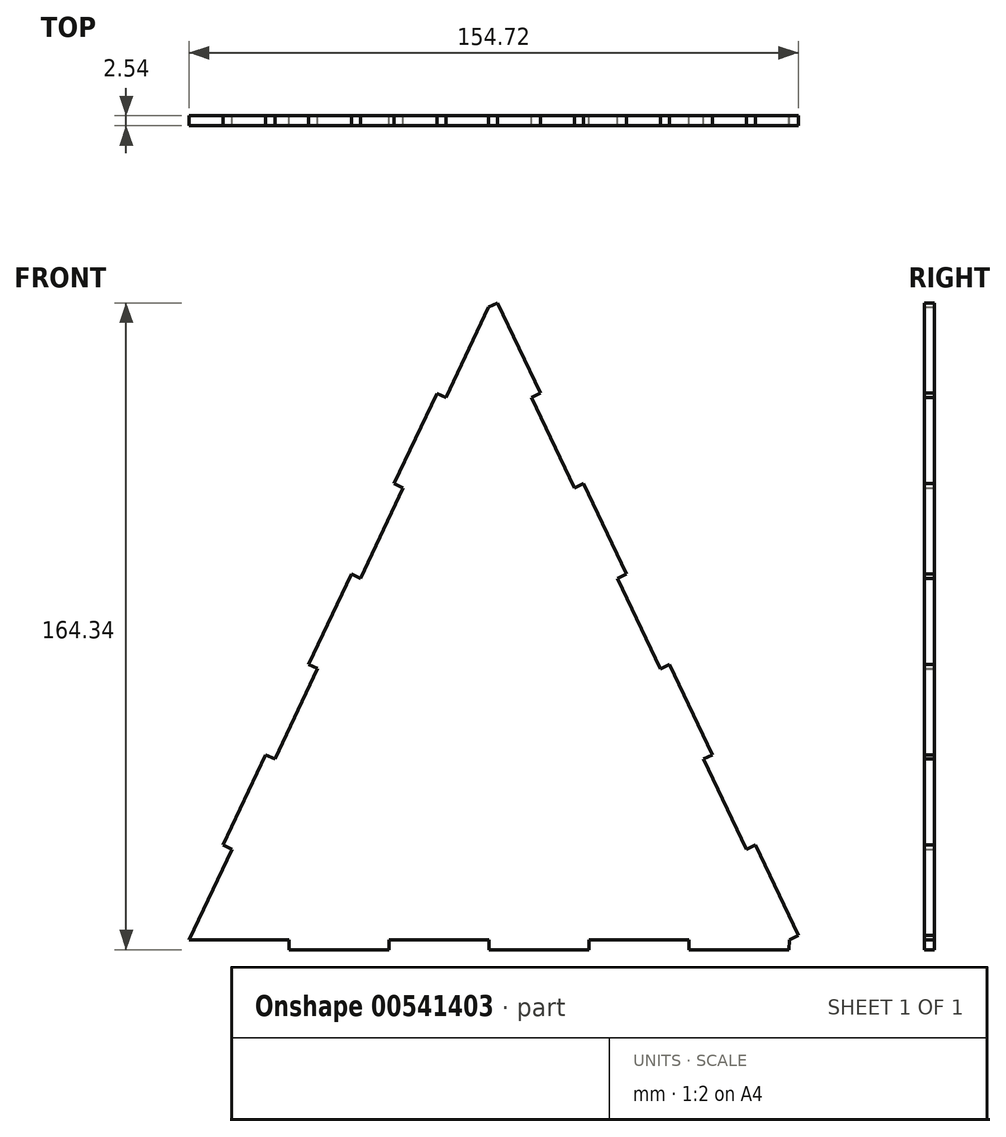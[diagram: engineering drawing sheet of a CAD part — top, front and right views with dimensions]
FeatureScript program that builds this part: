
annotation { "Feature Type Name" : "Feature", "Feature Type Description" : "" }
export const myFeature = defineFeature(function(context is Context, id is Id, definition is map)
    precondition{}
    {
        {
            var Q0;
            Q0=qCreatedBy(makeId("Front.planeOp"),FACE);
            var sketch = newSketch(context, id + "F0", { "sketchPlane" : qUnion([Q0])});
            skLineSegment(sketch, "E0", {"start": v(0, 85.84) * mm, "end": v(-76.07, -74.87) * mm});
            skLineSegment(sketch, "E1", {"start": v(-76.07, -74.87) * mm, "end": v(76.36, -74.87) * mm});
            skLineSegment(sketch, "E2", {"start": v(65.46, -51.93) * mm, "end": v(32.75, 16.9) * mm});
            skLineSegment(sketch, "E3", {"start": v(0, 85.84) * mm, "end": v(-10.87, 62.88) * mm});
            skLineSegment(sketch, "E4", {"start": v(-10.87, 62.88) * mm, "end": v(-13.16, 63.97) * mm});
            skLineSegment(sketch, "E5", {"start": v(-13.16, 63.97) * mm, "end": v(-24.03, 41) * mm});
            skLineSegment(sketch, "E6", {"start": v(-24.03, 41) * mm, "end": v(-21.73, 39.92) * mm});
            skLineSegment(sketch, "E7", {"start": v(-21.73, 39.92) * mm, "end": v(-32.6, 16.96) * mm});
            skLineSegment(sketch, "E8", {"start": v(-32.6, 16.96) * mm, "end": v(-34.9, 18.05) * mm});
            skLineSegment(sketch, "E9", {"start": v(-34.9, 18.05) * mm, "end": v(-45.76, -4.9) * mm});
            skLineSegment(sketch, "E10", {"start": v(-45.76, -4.9) * mm, "end": v(-43.47, -6) * mm});
            skLineSegment(sketch, "E11", {"start": v(-43.47, -6) * mm, "end": v(-54.33, -28.95) * mm});
            skLineSegment(sketch, "E12", {"start": v(-54.33, -28.95) * mm, "end": v(-56.63, -27.87) * mm});
            skLineSegment(sketch, "E13", {"start": v(-56.63, -27.87) * mm, "end": v(-67.5, -50.82) * mm});
            skLineSegment(sketch, "E14", {"start": v(-67.5, -50.82) * mm, "end": v(-65.2, -51.91) * mm});
            skLineSegment(sketch, "E15", {"start": v(-65.2, -51.91) * mm, "end": v(-76.07, -74.87) * mm});
            skLineSegment(sketch, "E16", {"start": v(21.8, 39.95) * mm, "end": v(32.75, 16.9) * mm});
            skLineSegment(sketch, "E17.trimOffspring", {"start": v(21.8, 39.95) * mm, "end": v(0, 85.84) * mm});
            skLineSegment(sketch, "E18", {"start": v(0, 85.84) * mm, "end": v(2.3, 86.93) * mm});
            skLineSegment(sketch, "E19", {"start": v(2.3, 86.93) * mm, "end": v(13.2, 63.99) * mm});
            skLineSegment(sketch, "E20", {"start": v(13.2, 63.99) * mm, "end": v(10.9, 62.9) * mm});
            skLineSegment(sketch, "E21", {"start": v(21.8, 39.95) * mm, "end": v(24.1, 41.04) * mm});
            skLineSegment(sketch, "E22", {"start": v(24.1, 41.04) * mm, "end": v(35, 18.1) * mm});
            skLineSegment(sketch, "E23", {"start": v(35, 18.1) * mm, "end": v(32.75, 16.9) * mm});
            skLineSegment(sketch, "E24", {"start": v(32.75, 16.9) * mm, "end": v(43.65, -6.04) * mm});
            skLineSegment(sketch, "E25", {"start": v(43.65, -6.04) * mm, "end": v(45.95, -4.95) * mm});
            skLineSegment(sketch, "E26", {"start": v(45.95, -4.95) * mm, "end": v(56.85, -27.9) * mm});
            skLineSegment(sketch, "E27", {"start": v(56.85, -27.9) * mm, "end": v(54.56, -28.98) * mm});
            skLineSegment(sketch, "E28", {"start": v(54.56, -28.98) * mm, "end": v(65.46, -51.93) * mm});
            skLineSegment(sketch, "E29", {"start": v(76.36, -74.87) * mm, "end": v(78.65, -73.78) * mm});
            skLineSegment(sketch, "E30", {"start": v(65.46, -51.93) * mm, "end": v(76.36, -74.87) * mm});
            skLineSegment(sketch, "E31", {"start": v(65.46, -51.93) * mm, "end": v(67.75, -50.84) * mm});
            skLineSegment(sketch, "E32", {"start": v(67.75, -50.84) * mm, "end": v(78.65, -73.78) * mm});
            skLineSegment(sketch, "E33", {"start": v(-76.07, -74.87) * mm, "end": v(-50.67, -74.87) * mm});
            skLineSegment(sketch, "E34", {"start": v(-50.67, -74.87) * mm, "end": v(-50.67, -77.4) * mm});
            skLineSegment(sketch, "E35", {"start": v(-50.67, -77.4) * mm, "end": v(-25.27, -77.4) * mm});
            skLineSegment(sketch, "E36", {"start": v(-25.27, -77.4) * mm, "end": v(-25.27, -74.87) * mm});
            skLineSegment(sketch, "E37", {"start": v(-25.27, -74.87) * mm, "end": v(0.13, -74.87) * mm});
            skLineSegment(sketch, "E38", {"start": v(0.13, -74.87) * mm, "end": v(0.13, -77.4) * mm});
            skLineSegment(sketch, "E39", {"start": v(0.13, -77.4) * mm, "end": v(25.53, -77.4) * mm});
            skLineSegment(sketch, "E40", {"start": v(25.53, -77.4) * mm, "end": v(25.53, -74.87) * mm});
            skLineSegment(sketch, "E41", {"start": v(25.53, -74.87) * mm, "end": v(50.93, -74.87) * mm});
            skLineSegment(sketch, "E42", {"start": v(50.93, -74.87) * mm, "end": v(50.93, -77.4) * mm});
            skLineSegment(sketch, "E43", {"start": v(50.93, -77.4) * mm, "end": v(76.33, -77.4) * mm});
            skLineSegment(sketch, "E44", {"start": v(76.33, -77.4) * mm, "end": v(76.36, -74.87) * mm});
            skSolve(sketch);
        }
        {
            var Q0;
            Q0=qSketchRegion(id+"F0",true);
            extrude(context, id + "F1", {"entities" : qUnion([Q0]), "depth" : 2.54 * mm, "offsetDistance" : 25.4 * mm});
        }
    });
